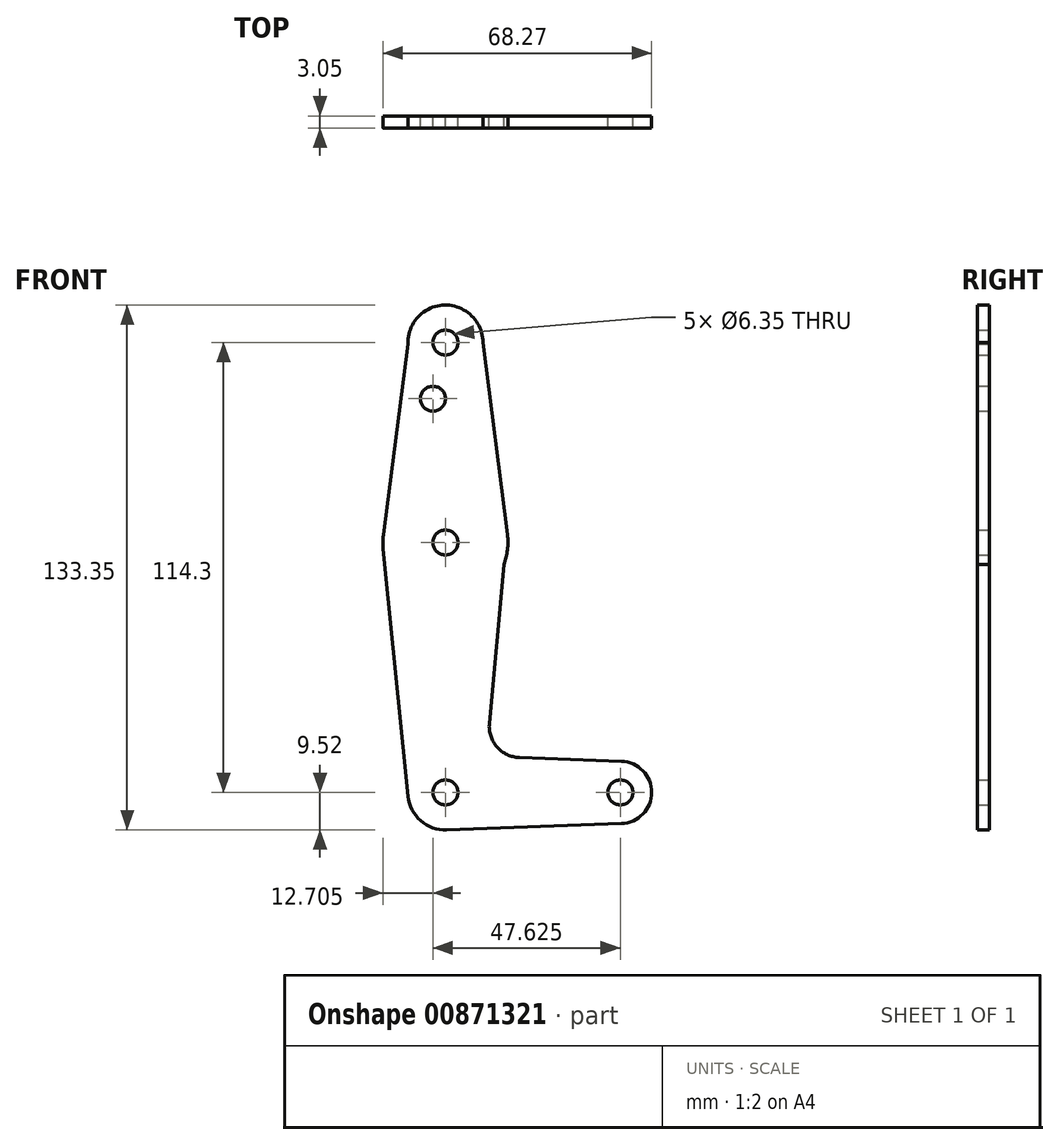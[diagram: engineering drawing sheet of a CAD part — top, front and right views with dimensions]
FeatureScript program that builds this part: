
annotation { "Feature Type Name" : "Feature", "Feature Type Description" : "" }
export const myFeature = defineFeature(function(context is Context, id is Id, definition is map)
    precondition{}
    {
        {
            var Q0;
            Q0=qCreatedBy(makeId("Front.planeOp"),FACE);
            var sketch = newSketch(context, id + "F0", { "sketchPlane" : qUnion([Q0])});
            skLineSegment(sketch, "E0", {"start": v(0, 114.3) * mm, "end": v(0, 0) * mm, "construction": true});
            skLineSegment(sketch, "E1", {"start": v(0, 0) * mm, "end": v(44.45, 0) * mm, "construction": true});
            skCircle(sketch, "E2", {"center": v(0, 114.3) * mm, "radius": 9.53 * mm});
            skCircle(sketch, "E3", {"center": v(0, 63.5) * mm, "radius": 15.88 * mm});
            skCircle(sketch, "E4", {"center": v(0, 0) * mm, "radius": 9.53 * mm});
            skCircle(sketch, "E5", {"center": v(44.45, 0) * mm, "radius": 7.94 * mm});
            skLineSegment(sketch, "E6", {"start": v(-9.52, 113.92) * mm, "end": v(-15.75, 65.53) * mm});
            skLineSegment(sketch, "E7", {"start": v(9.53, 114.3) * mm, "end": v(15.75, 65.5) * mm});
            skCircle(sketch, "E8", {"center": v(-3.17, 100.03) * mm, "radius": 3.18 * mm});
            skCircle(sketch, "E9", {"center": v(0, 114.3) * mm, "radius": 3.18 * mm});
            skCircle(sketch, "E10", {"center": v(0, 63.5) * mm, "radius": 3.18 * mm});
            skLineSegment(sketch, "E11", {"start": v(-15.8, 61.91) * mm, "end": v(-9.48, -0.95) * mm});
            skLineSegment(sketch, "E12", {"start": v(44.73, -7.93) * mm, "end": v(0.34, -9.52) * mm});
            skLineSegment(sketch, "E13", {"start": v(18.8, 8.86) * mm, "end": v(44.73, 7.93) * mm});
            skLineSegment(sketch, "E14", {"start": v(14.85, 57.89) * mm, "end": v(11.16, 17.53) * mm});
            skCircle(sketch, "E15", {"center": v(44.45, 0) * mm, "radius": 3.18 * mm});
            skCircle(sketch, "E16", {"center": v(0, 0) * mm, "radius": 3.18 * mm});
            skArc(sketch, "E17.filletArc", {"start": v(11.16, 17.53) * mm, "mid": v(13.12, 11.55) * mm, "end": v(18.8, 8.86) * mm});
            skSolve(sketch);
        }
        {
            var Q0;
            Q0 = qSketchRegion(id + "F0", true);
            extrude(context, id + "F1", {"entities" : qUnion([Q0]), "depth" : 3.05 * mm, "offsetDistance" : 25.4 * mm});
        }
    });
